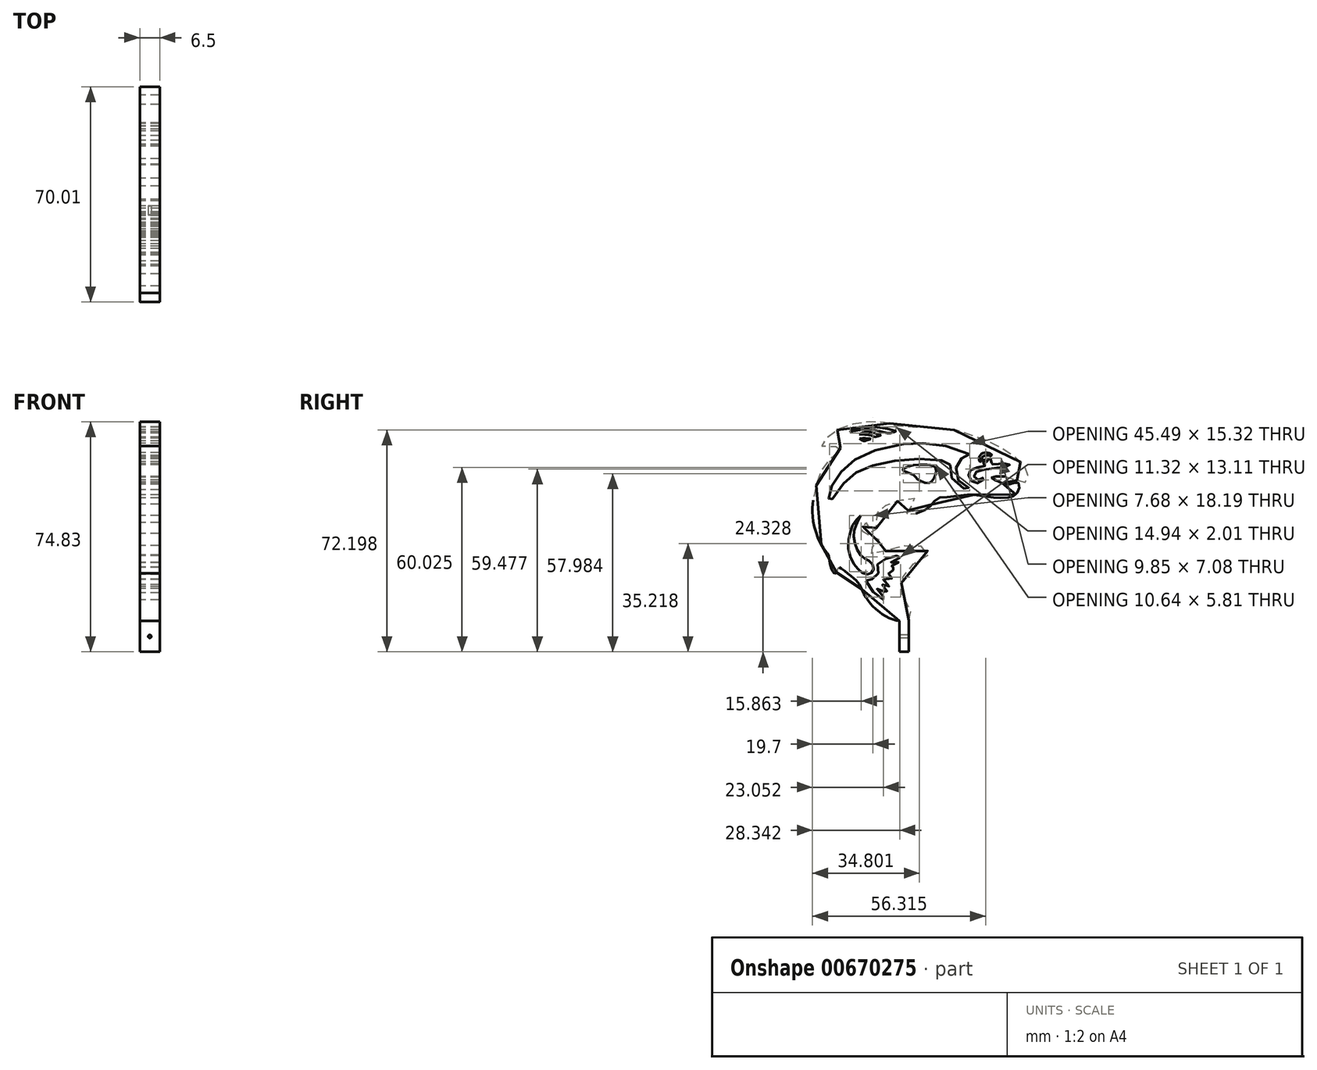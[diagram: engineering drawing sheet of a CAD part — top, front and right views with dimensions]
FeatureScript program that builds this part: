
annotation { "Feature Type Name" : "Feature", "Feature Type Description" : "" }
export const myFeature = defineFeature(function(context is Context, id is Id, definition is map)
    precondition{}
    {
        {
            var Q0;
            Q0=qCreatedBy(makeId("Right.planeOp"),FACE);
            var sketch = newSketch(context, id + "F0", { "sketchPlane" : qUnion([Q0])});
            skFitSpline(sketch, "E0", {"points": [v(11.7, 19.2) * mm, v(11.52, 17.45) * mm, v(11.88, 15.78) * mm, v(13, 13.88) * mm, v(15.12, 12.13) * mm, v(16.84, 11.23) * mm, v(17.92, 11.1) * mm, v(18.15, 11.23) * mm, v(18.15, 11.45) * mm, v(17.6, 11.86) * mm, v(16.48, 12.53) * mm, v(14.94, 13.57) * mm, v(14.04, 14.83) * mm, v(13.6, 16.44) * mm, v(13.61, 18.05) * mm, v(13.87, 19.57) * mm, v(14.44, 20.5) * mm, v(15.21, 21.2) * mm, v(16.68, 21.86) * mm, v(17.48, 22.17) * mm, v(17.9, 22.45) * mm, v(17.93, 22.66) * mm, v(17.69, 23) * mm, v(10.03, 25.37) * mm, v(4.2, 26.12) * mm, v(1, 26.23) * mm, v(-2.73, 26.08) * mm, v(-10.02, 24.79) * mm, v(-17, 22.13) * mm, v(-19.57, 20.64) * mm, v(-21.88, 18.86) * mm, v(-24.35, 16.18) * mm, v(-25.9, 14.02) * mm, v(-27.11, 11.68) * mm, v(-27.64, 10.08) * mm, v(-27.82, 8.69) * mm, v(-27.61, 7.02) * mm, v(-27.37, 6.36) * mm, v(-27.2, 6.81) * mm, v(-25.4, 10.47) * mm, v(-23.49, 12.7) * mm, v(-20.84, 15.27) * mm, v(-19.54, 16.25) * mm, v(-16.44, 18) * mm, v(-13.86, 18.94) * mm, v(-8.84, 20.02) * mm, v(-4.45, 20.76) * mm, v(1.76, 21.18) * mm, v(6.53, 20.84) * mm, v(10.5, 20.35) * mm, v(11.2, 20.11) * mm, v(11.58, 19.83) * mm, v(11.7, 19.2) * mm]});
            skFitSpline(sketch, "E1", {"points": [v(2.97, 19.27) * mm, v(4.54, 19.2) * mm, v(5.62, 19) * mm, v(6.38, 18.79) * mm, v(7.01, 18.23) * mm, v(7.11, 17.3) * mm, v(6.87, 15.66) * mm, v(5.89, 13.98) * mm, v(4.8, 13.32) * mm, v(3.03, 13.53) * mm, v(1.29, 14.47) * mm, v(0.7, 14.92) * mm, v(0, 15.82) * mm, v(-0.77, 16.24) * mm, v(-2.44, 16.86) * mm, v(-3.48, 17.25) * mm, v(-3.76, 17.56) * mm, v(-3.3, 17.94) * mm, v(-1.91, 18.64) * mm, v(0.39, 19.13) * mm, v(2.97, 19.27) * mm]});
            skFitSpline(sketch, "E2", {"points": [v(22.88, 22.22) * mm, v(23.75, 22.29) * mm, v(24.62, 22.11) * mm, v(24.93, 22.07) * mm, v(25.12, 22.18) * mm, v(25.19, 22.34) * mm, v(25.1, 22.6) * mm, v(24.77, 22.89) * mm, v(24.22, 23.1) * mm, v(23.35, 23.23) * mm, v(22.5, 23.09) * mm, v(21.75, 22.62) * mm, v(21.23, 21.94) * mm, v(21.07, 21.08) * mm, v(21.26, 20.44) * mm, v(21.42, 20.27) * mm, v(21.54, 20.2) * mm, v(21.67, 20.25) * mm, v(21.76, 20.48) * mm, v(21.89, 21.14) * mm, v(22.34, 21.83) * mm, v(22.88, 22.22) * mm]});
            skFitSpline(sketch, "E3", {"points": [v(22.95, 21.15) * mm, v(22.76, 20.98) * mm, v(22.57, 20.59) * mm, v(22.53, 20.1) * mm, v(22.7, 19.61) * mm, v(23.08, 19.2) * mm, v(23.16, 19.04) * mm, v(23.14, 18.88) * mm, v(22.52, 18.75) * mm, v(21.1, 18.54) * mm, v(19.63, 18.13) * mm, v(18.56, 17.58) * mm, v(18.06, 17.2) * mm, v(17.73, 16.64) * mm, v(17.65, 15.83) * mm, v(17.83, 15.13) * mm, v(18.43, 14.2) * mm, v(19.16, 13.6) * mm, v(19.94, 13.27) * mm, v(20.94, 13.25) * mm, v(21.96, 13.72) * mm, v(22.4, 14.18) * mm, v(22.55, 14.55) * mm, v(22.54, 14.93) * mm, v(22.46, 15.12) * mm, v(22.37, 15.08) * mm, v(22.15, 14.75) * mm, v(21.67, 14.4) * mm, v(21.2, 14.28) * mm, v(20.38, 14.33) * mm, v(19.86, 14.68) * mm, v(19.53, 15.4) * mm, v(19.6, 16.11) * mm, v(19.8, 16.5) * mm, v(20.22, 16.9) * mm, v(20.88, 17.2) * mm, v(22.14, 17.56) * mm, v(26.26, 18.2) * mm, v(28.53, 18.35) * mm, v(29.53, 18.45) * mm, v(30.2, 18.64) * mm, v(30.72, 18.9) * mm, v(31.06, 19.2) * mm, v(31.16, 19.4) * mm, v(31.13, 19.56) * mm, v(30.87, 19.64) * mm, v(26.57, 19.47) * mm, v(25.57, 19.32) * mm, v(25.17, 19.26) * mm, v(25.02, 19.3) * mm, v(24.99, 19.47) * mm, v(25.1, 19.76) * mm, v(25.13, 20.15) * mm, v(25.12, 20.68) * mm, v(24.96, 21.07) * mm, v(24.71, 21.38) * mm, v(24.43, 21.47) * mm, v(24.08, 21.44) * mm, v(24.1, 21.18) * mm, v(24.19, 21.06) * mm, v(24.24, 20.73) * mm, v(24.15, 20.43) * mm, v(23.92, 20.27) * mm, v(23.63, 20.24) * mm, v(23.32, 20.38) * mm, v(23.13, 20.56) * mm, v(23.03, 20.88) * mm, v(22.95, 21.15) * mm]});
            skFitSpline(sketch, "E4", {"points": [v(-17.7, 27.7) * mm, v(-16.98, 27.23) * mm, v(-16.5, 27.03) * mm, v(-16.01, 27) * mm, v(-15.44, 27.15) * mm, v(-14.27, 27.57) * mm, v(-14.18, 27.62) * mm, v(-14.18, 27.67) * mm, v(-14.3, 27.69) * mm, v(-14.76, 27.72) * mm, v(-15.4, 27.78) * mm, v(-16.07, 27.83) * mm, v(-16.85, 27.8) * mm, v(-17.7, 27.7) * mm]});
            skFitSpline(sketch, "E5", {"points": [v(-17.83, 29.2) * mm, v(-16.35, 29.1) * mm, v(-15.2, 28.97) * mm, v(-14.13, 28.76) * mm, v(-13.52, 28.58) * mm, v(-13.02, 28.38) * mm, v(-12.85, 28.32) * mm, v(-12.52, 28.31) * mm, v(-12.35, 28.35) * mm, v(-11.9, 28.5) * mm, v(-10.8, 28.78) * mm, v(-10.8, 28.8) * mm, v(-11.25, 29) * mm, v(-12.24, 29.34) * mm, v(-13.05, 29.58) * mm, v(-13.83, 29.76) * mm, v(-14.68, 29.83) * mm, v(-15.65, 29.82) * mm, v(-16.53, 29.7) * mm, v(-17.22, 29.46) * mm, v(-17.83, 29.2) * mm]});
            skFitSpline(sketch, "E6", {"points": [v(-20.83, 30.32) * mm, v(-20.89, 30.24) * mm, v(-20.87, 30.16) * mm, v(-20.75, 30.1) * mm, v(-19.47, 30.28) * mm, v(-17.87, 30.53) * mm, v(-16.3, 30.65) * mm, v(-14.16, 30.65) * mm, v(-11.9, 30.38) * mm, v(-10.58, 30.01) * mm, v(-9.14, 29.6) * mm, v(-8.7, 29.52) * mm, v(-7.99, 29.54) * mm, v(-6.78, 29.77) * mm, v(-5.86, 30.04) * mm, v(-5.85, 30.07) * mm, v(-6.16, 30.17) * mm, v(-7.52, 30.6) * mm, v(-9.12, 31) * mm, v(-11.14, 31.33) * mm, v(-13.27, 31.55) * mm, v(-14.21, 31.6) * mm, v(-15.58, 31.6) * mm, v(-17.26, 31.45) * mm, v(-18.46, 31.21) * mm, v(-19.35, 30.97) * mm, v(-20.23, 30.66) * mm, v(-20.83, 30.32) * mm]});
            skFitSpline(sketch, "E7", {"points": [v(-17.32, 2.7) * mm, v(-18.85, 1.3) * mm, v(-20.06, -0.54) * mm, v(-20.76, -2.65) * mm, v(-21.41, -6.65) * mm, v(-20.92, -10.4) * mm, v(-19.44, -13.3) * mm, v(-17.94, -15) * mm, v(-16.58, -16.02) * mm, v(-15.23, -16.4) * mm, v(-14.35, -16.25) * mm, v(-13.42, -15.51) * mm, v(-13.14, -14.5) * mm, v(-13.54, -13.17) * mm, v(-14.38, -12.21) * mm, v(-15.42, -11.62) * mm, v(-16.55, -10.9) * mm, v(-17.57, -9.9) * mm, v(-18.73, -7.94) * mm, v(-19.52, -5.4) * mm, v(-19.67, -3.22) * mm, v(-19.28, -1.47) * mm, v(-18.73, 0.2) * mm, v(-17.86, 1.83) * mm, v(-17.32, 2.7) * mm]});
            skFitSpline(sketch, "E8", {"points": [v(-15.67, -18.5) * mm, v(-14.85, -20.12) * mm, v(-13.62, -21.74) * mm, v(-12.36, -23.08) * mm, v(-10.89, -24.2) * mm, v(-10.11, -24.6) * mm, v(-9.66, -24.75) * mm, v(-9.4, -24.73) * mm, v(-9.36, -24.57) * mm, v(-9.63, -24.08) * mm, v(-10.28, -23.33) * mm, v(-11.16, -22.3) * mm, v(-11.74, -21.62) * mm, v(-12.01, -21.24) * mm, v(-12.08, -21.08) * mm, v(-12.06, -21) * mm, v(-11.95, -20.98) * mm, v(-11.02, -21.4) * mm, v(-9.75, -22.05) * mm, v(-9.18, -22.29) * mm, v(-8.85, -22.4) * mm, v(-8.64, -22.42) * mm, v(-8.52, -22.4) * mm, v(-8.54, -22.26) * mm, v(-8.88, -21.81) * mm, v(-9.61, -21.01) * mm, v(-10.22, -20.17) * mm, v(-10.32, -19.92) * mm, v(-10.34, -19.8) * mm, v(-10.32, -19.73) * mm, v(-10.23, -19.72) * mm, v(-9.35, -20.14) * mm, v(-8.82, -20.3) * mm, v(-8.33, -20.34) * mm, v(-8.14, -20.23) * mm, v(-8.12, -20.01) * mm, v(-8.26, -19.76) * mm, v(-9.85, -18.3) * mm, v(-10, -18.13) * mm, v(-9.96, -18) * mm, v(-9.77, -17.94) * mm, v(-7.8, -17.94) * mm, v(-7.4, -17.85) * mm, v(-7.19, -17.72) * mm, v(-7.14, -17.5) * mm, v(-7.27, -17.3) * mm, v(-7.57, -16.95) * mm, v(-8.12, -16.38) * mm, v(-8.31, -16.14) * mm, v(-8.44, -15.86) * mm, v(-8.4, -15.61) * mm, v(-8.1, -15.38) * mm, v(-7.35, -15.12) * mm, v(-6.62, -15.03) * mm, v(-6.42, -15) * mm, v(-6.34, -14.93) * mm, v(-6.32, -14.8) * mm, v(-6.32, -14.5) * mm, v(-6.5, -14.3) * mm, v(-6.81, -14.13) * mm, v(-7.33, -14.05) * mm, v(-7.68, -14) * mm, v(-8.1, -14.02) * mm, v(-8.14, -13.98) * mm, v(-8.1, -13.93) * mm, v(-6.6, -13.48) * mm, v(-5.56, -13.03) * mm, v(-5.14, -12.77) * mm, v(-5.03, -12.65) * mm, v(-5.02, -12.52) * mm, v(-5.75, -12.52) * mm, v(-6.3, -12.58) * mm, v(-6.92, -12.58) * mm, v(-7.37, -12.53) * mm, v(-7.48, -12.4) * mm, v(-7.44, -12.27) * mm, v(-5.76, -11.52) * mm, v(-4.65, -11) * mm, v(-4.56, -10.93) * mm, v(-4.4, -10.8) * mm, v(-4.31, -10.65) * mm, v(-4.36, -10.47) * mm, v(-4.7, -10.38) * mm, v(-5.16, -10.35) * mm, v(-6.18, -10.49) * mm, v(-7.63, -10.82) * mm, v(-9.15, -11.38) * mm, v(-9.95, -11.78) * mm, v(-10.87, -12.39) * mm, v(-11.7, -13.08) * mm, v(-11.95, -13.32) * mm, v(-11.87, -13.51) * mm, v(-11.6, -14.44) * mm, v(-11.6, -15.79) * mm, v(-12.06, -16.98) * mm, v(-12.85, -17.75) * mm, v(-13.42, -17.97) * mm, v(-13.9, -18.05) * mm, v(-15.21, -18.07) * mm, v(-15.4, -18.1) * mm, v(-15.6, -18.18) * mm, v(-15.69, -18.34) * mm, v(-15.67, -18.5) * mm]});
            skFitSpline(sketch, "E9", {"points": [v(-9.97, -29.58) * mm, v(-8.03, -30.67) * mm, v(-6.3, -31.25) * mm, v(-4.77, -31.62) * mm, v(-3.75, -31.64) * mm, v(-2.56, -31.57) * mm, v(-1.13, -31.33) * mm, v(-0.26, -31.04) * mm, v(-0.24, -31.02) * mm, v(-0.37, -30.63) * mm, v(-0.67, -29.72) * mm, v(-1.06, -28.52) * mm, v(-2.15, -26.6) * mm, v(-3.19, -24.8) * mm, v(-3.95, -22.91) * mm, v(-4.2, -21.55) * mm, v(-4.24, -20.23) * mm, v(-3.9, -18.2) * mm, v(-3.31, -16.48) * mm, v(-2.7, -15.2) * mm, v(-1.74, -14.04) * mm, v(0.1, -12.82) * mm, v(2.68, -11.42) * mm, v(4.07, -10.65) * mm, v(4.38, -10.34) * mm, v(4.6, -10.01) * mm, v(4.6, -9.41) * mm, v(4.36, -8.73) * mm, v(3.93, -8.13) * mm, v(3.37, -7.76) * mm, v(2.13, -7.32) * mm, v(1.22, -7.18) * mm, v(0.12, -7.03) * mm, v(-1.76, -7.05) * mm, v(-3.95, -7.22) * mm, v(-5.83, -7.6) * mm, v(-7.34, -8.09) * mm, v(-9.56, -8.98) * mm, v(-11.02, -9.66) * mm, v(-12.24, -10.03) * mm, v(-13.3, -9.95) * mm, v(-14.1, -9.5) * mm, v(-14.6, -9.02) * mm, v(-14.84, -8.76) * mm, v(-14.9, -8.59) * mm, v(-14.83, -8.45) * mm, v(-14.5, -8.15) * mm, v(-13.6, -7.55) * mm, v(-12.9, -7.08) * mm, v(-12.37, -6.67) * mm, v(-11.94, -6.17) * mm, v(-11.63, -5.76) * mm, v(-11.44, -5.37) * mm, v(-11.39, -5.2) * mm, v(-11.38, -4.88) * mm, v(-11.43, -4.75) * mm, v(-11.7, -4.52) * mm, v(-12.2, -4.31) * mm, v(-13.1, -4.11) * mm, v(-14.08, -3.96) * mm, v(-14.93, -3.84) * mm, v(-16.04, -3.7) * mm, v(-16.52, -3.48) * mm, v(-16.74, -3.25) * mm, v(-16.92, -2.9) * mm, v(-16.96, -2.28) * mm, v(-16.9, -1.86) * mm, v(-16.72, -1.07) * mm, v(-16.36, -0.23) * mm, v(-16.1, 0.2) * mm, v(-15.96, 0.4) * mm, v(-15.85, 0.47) * mm, v(-15.7, 0.48) * mm, v(-15.56, 0.37) * mm, v(-15.37, 0.06) * mm, v(-14.9, -0.9) * mm, v(-14.44, -1.82) * mm, v(-14.08, -2.34) * mm, v(-13.81, -2.67) * mm, v(-13.52, -2.96) * mm, v(-13.32, -3.07) * mm, v(-13.13, -3.1) * mm, v(-12.88, -3.05) * mm, v(-12.66, -2.77) * mm, v(-12.45, -2.24) * mm, v(-12.29, -1.49) * mm, v(-12.16, -0.63) * mm, v(-12.05, 0.44) * mm, v(-11.99, 2.57) * mm, v(-11.92, 3.65) * mm, v(-11.77, 4.2) * mm, v(-11.52, 4.6) * mm, v(-10.96, 5.15) * mm, v(-10.07, 5.68) * mm, v(-9.1, 6.17) * mm, v(-7.95, 6.7) * mm, v(-6.69, 7.02) * mm, v(-4.55, 7.6) * mm, v(-3.05, 7.98) * mm, v(-1.72, 8.26) * mm, v(-1.05, 8.37) * mm, v(-0.47, 8.42) * mm, v(-0.12, 8.4) * mm, v(0.13, 8.3) * mm, v(0.23, 8.24) * mm, v(0.3, 8.1) * mm, v(0.28, 7.85) * mm, v(0.17, 7.52) * mm, v(-0.1, 7.03) * mm, v(-0.64, 6.17) * mm, v(-1.12, 5.4) * mm, v(-1.58, 4.8) * mm, v(-2.08, 4.25) * mm, v(-2.4, 3.93) * mm, v(-2.57, 3.69) * mm, v(-2.61, 3.38) * mm, v(-2.55, 3.13) * mm, v(-2.34, 2.95) * mm, v(-2.04, 2.8) * mm, v(-1.72, 2.75) * mm, v(-1.07, 2.84) * mm, v(-0.46, 3.04) * mm, v(0.27, 3.32) * mm, v(2.62, 4.23) * mm, v(3.86, 4.77) * mm, v(4.65, 5.28) * mm, v(5.3, 5.83) * mm, v(6.19, 6.87) * mm, v(6.85, 7.65) * mm, v(7.45, 8.15) * mm, v(8.28, 8.53) * mm, v(9.06, 8.64) * mm, v(10.9, 8.77) * mm, v(13.4, 8.97) * mm, v(16.4, 9.33) * mm, v(17.91, 9.43) * mm, v(18.71, 9.48) * mm, v(19.91, 9.44) * mm, v(21.08, 9.3) * mm, v(24.9, 8.7) * mm, v(26.2, 8.56) * mm, v(27.16, 8.5) * mm, v(28.64, 8.45) * mm, v(30.24, 8.49) * mm, v(30.98, 8.61) * mm, v(31.7, 8.82) * mm, v(32.37, 9.14) * mm, v(32.94, 9.5) * mm, v(33.33, 9.85) * mm, v(33.85, 10.63) * mm, v(34.09, 11.18) * mm, v(34.21, 11.74) * mm, v(34.24, 12.6) * mm, v(34.1, 13.07) * mm, v(33.92, 13.33) * mm, v(33.59, 13.56) * mm, v(33.36, 13.6) * mm, v(32.84, 13.5) * mm, v(32.34, 13.31) * mm, v(31.6, 13.06) * mm, v(31, 12.9) * mm, v(29.92, 12.9) * mm, v(28.8, 13.17) * mm, v(27.84, 13.54) * mm, v(26.27, 14.26) * mm, v(25.53, 14.69) * mm, v(25.23, 14.97) * mm, v(25.18, 15.1) * mm, v(25.24, 15.21) * mm, v(25.57, 15.35) * mm, v(26.5, 15.45) * mm, v(28.53, 15.47) * mm, v(29.94, 15.3) * mm, v(31.13, 15.03) * mm, v(32.48, 14.57) * mm, v(33.85, 14.02) * mm, v(34.85, 13.6) * mm, v(35.38, 13.46) * mm, v(35.9, 13.44) * mm, v(36.25, 13.57) * mm, v(36.58, 13.89) * mm, v(36.8, 14.32) * mm, v(36.94, 15.05) * mm, v(36.94, 15.87) * mm, v(36.9, 16.14) * mm, v(36.78, 16.73) * mm, v(36.57, 17.42) * mm, v(36.04, 18.43) * mm, v(35.55, 19.14) * mm, v(34.16, 20.6) * mm, v(31.92, 22.37) * mm, v(29.4, 24.1) * mm, v(26.5, 25.76) * mm, v(24.87, 26.56) * mm, v(18.34, 29.1) * mm, v(11.88, 30.8) * mm, v(6.74, 31.46) * mm, v(3.35, 31.55) * mm, v(-1.28, 31.45) * mm, v(-4.38, 31.56) * mm, v(-5.77, 31.85) * mm, v(-7.07, 32.35) * mm, v(-8.2, 32.7) * mm, v(-9.8, 33) * mm, v(-11.62, 33.18) * mm, v(-14.28, 33.18) * mm, v(-15.99, 33.03) * mm, v(-19.34, 32.52) * mm, v(-21.19, 32.08) * mm, v(-22.4, 31.7) * mm, v(-25.11, 30.51) * mm, v(-27.07, 29.25) * mm, v(-28.6, 27.82) * mm, v(-29.44, 26.71) * mm, v(-30.15, 25.5) * mm, v(-30.18, 25.43) * mm, v(-30.17, 25.4) * mm, v(-30.03, 25.38) * mm, v(-28.05, 25.4) * mm, v(-26.2, 25.25) * mm, v(-25, 25.07) * mm, v(-24.41, 24.9) * mm, v(-24.08, 24.71) * mm, v(-23.96, 24.6) * mm, v(-23.93, 24.36) * mm, v(-23.99, 24.17) * mm, v(-24.62, 23.5) * mm, v(-26.66, 21.77) * mm, v(-28.3, 20.09) * mm, v(-29.13, 19.01) * mm, v(-30.34, 17.18) * mm, v(-30.64, 16.28) * mm, v(-31.35, 14.13) * mm, v(-31.72, 12.86) * mm, v(-32.3, 10.62) * mm, v(-32.9, 7.3) * mm, v(-33.04, 5.68) * mm, v(-33.04, 3.16) * mm, v(-32.68, 0.2) * mm, v(-31.5, -4.06) * mm, v(-30.66, -6) * mm, v(-29.58, -7.8) * mm, v(-28.73, -8.9) * mm, v(-28, -9.9) * mm, v(-27.68, -10.7) * mm, v(-27.57, -11.56) * mm, v(-27.5, -12.5) * mm, v(-27.25, -13.66) * mm, v(-26.9, -14.6) * mm, v(-26.49, -15.38) * mm, v(-26.17, -15.78) * mm, v(-25.85, -16.04) * mm, v(-25.6, -16.09) * mm, v(-25.35, -16) * mm, v(-25.1, -15.64) * mm, v(-24.95, -15.23) * mm, v(-24.8, -14.67) * mm, v(-24.67, -14.33) * mm, v(-24.55, -14.23) * mm, v(-24.37, -14.19) * mm, v(-23.98, -14.34) * mm, v(-22.27, -15.57) * mm, v(-20.54, -16.99) * mm, v(-19.4, -17.93) * mm, v(-18.56, -18.71) * mm, v(-18.03, -19.36) * mm, v(-17.5, -20.28) * mm, v(-16.67, -22.09) * mm, v(-15.8, -23.7) * mm, v(-14.5, -25.62) * mm, v(-13.56, -26.71) * mm, v(-11.46, -28.57) * mm, v(-9.97, -29.58) * mm]});
            skLineSegment(sketch, "E10", {"start": v(-4.77, -31.62) * mm, "end": v(-4.77, -41.62) * mm});
            skLineSegment(sketch, "E11", {"start": v(-4.77, -41.62) * mm, "end": v(-1.77, -41.62) * mm});
            skLineSegment(sketch, "E12", {"start": v(-1.77, -41.62) * mm, "end": v(-1.77, -31.47) * mm});
            skLineSegment(sketch, "E13", {"start": v(-3.27, -41.62) * mm, "end": v(-3.27, -31.62) * mm});
            skLineSegment(sketch, "E14", {"start": v(-4.77, -36.54) * mm, "end": v(-1.77, -36.54) * mm});
            skPoint(sketch, "E14.startSnap0", {"position": v(-1.77, -36.54) * mm});
            skSolve(sketch);
        }
        {
            var Q0;
            Q0=makeQuery(id+"F0.imprint","IMPRINT",FACE,{"disambiguationData":[TD([[makeQuery(id+"F0.imprint","IMPRINT",EDGE,{"derivedFrom":sQuery(id+"F0.wireOp",EDGE,"E0")}),-1.0]])]});
            var Q1;
            {var subQ0=sQuery(id+"F0.wireOp",EDGE,"E10");Q1=makeQuery(id+"F0.imprint","IMPRINT",FACE,{"disambiguationData":[TD([[makeQuery(id+"F0.imprint","IMPRINT",EDGE,{"derivedFrom":subQ0}),1.0]])]});}
            var Q2;
            Q2=makeQuery(id+"F0.imprint","IMPRINT",FACE,{"disambiguationData":[TD([[makeQuery(id+"F0.imprint","IMPRINT",EDGE,{"derivedFrom":sQuery(id+"F0.wireOp",EDGE,"FLHJb7bR-lL8j-JZDz-AZfH-eIbeRFMx4ZKu")}),1.0]])]});
            var Q3;
            {var subQ4=sQuery(id+"F0.wireOp",EDGE,"E12");Q3=makeQuery(id+"F0.imprint","IMPRINT",FACE,{"disambiguationData":[TD([[makeQuery(id+"F0.imprint","IMPRINT",EDGE,{"derivedFrom":subQ4}),1.0]])]});}
            extrude(context, id + "F1", {"entities" : qUnion([Q0, Q1, Q2, Q3]), "depth" : 6.5 * mm, "offsetDistance" : 25 * mm});
        }
        {
            var Q0;
            Q0=makeQuery(id+"F1.opExtrude","SWEPT_FACE",FACE,{"disambiguationData":[OSD([sQuery(id+"F0.wireOp",EDGE,"E10")])]});
            var sketch = newSketch(context, id + "F2", { "sketchPlane" : qUnion([Q0])});
            skLineSegment(sketch, "E15", {"start": v(3.25, -41.62) * mm, "end": v(3.25, -31.62) * mm});
            skLineSegment(sketch, "E16", {"start": v(6.5, -36.62) * mm, "end": v(0, -36.62) * mm});
            skCircle(sketch, "E17", {"center": v(3.25, -36.62) * mm, "radius": 0.5 * mm});
            skSolve(sketch);
        }
        {
            var Q0;
            Q0 = qSketchRegion(id + "F2", true);
            extrude(context, id + "F3", {"entities" : qUnion([Q0]), "operationType" : NewBodyOperationType.REMOVE, "endBound" : BoundingType.THROUGH_ALL, "oppositeDirection" : true, "depth" : 25 * mm, "offsetDistance" : 25 * mm});
        }
    });
